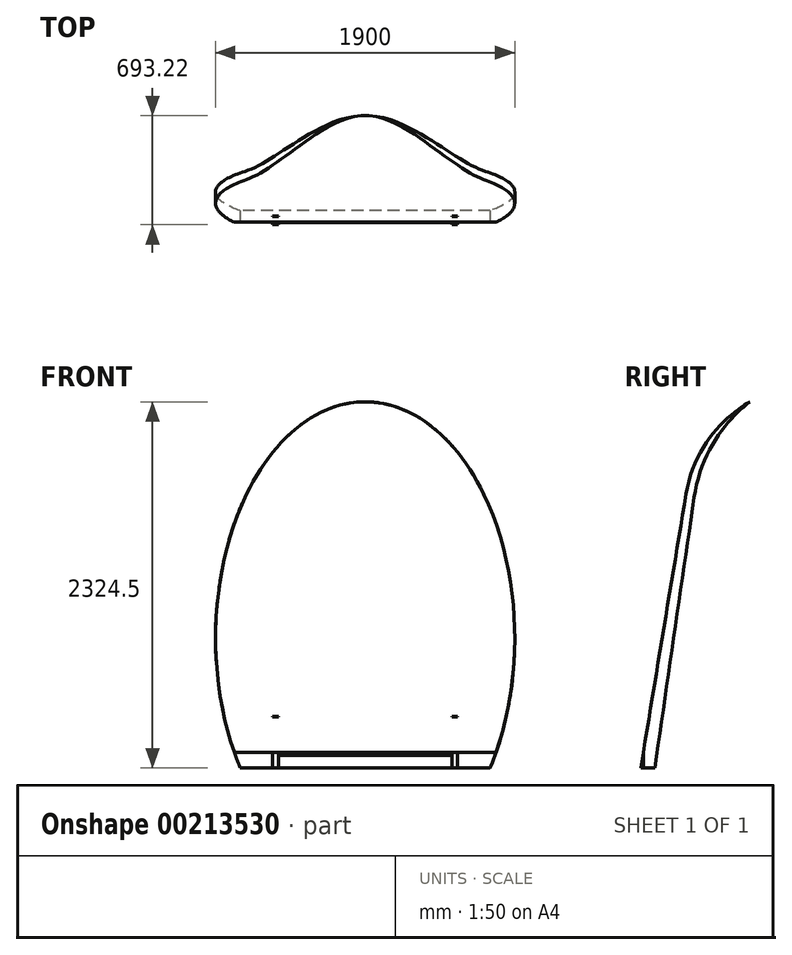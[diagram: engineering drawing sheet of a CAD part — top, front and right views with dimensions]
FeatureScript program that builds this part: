
annotation { "Feature Type Name" : "Feature", "Feature Type Description" : "" }
export const myFeature = defineFeature(function(context is Context, id is Id, definition is map)
    precondition{}
    {
        {
            var Q0;
            Q0=qCreatedBy(makeId("Top.planeOp"),FACE);
            var sketch = newSketch(context, id + "F0", { "sketchPlane" : qUnion([Q0])});
            skLineSegment(sketch, "E0.bottom", {"start": v(-1200, -1500) * mm, "end": v(-1150, -1500) * mm});
            skLineSegment(sketch, "E0.top", {"start": v(-1200, 1500) * mm, "end": v(-1150, 1500) * mm});
            skLineSegment(sketch, "E0.left", {"start": v(-1200, -1500) * mm, "end": v(-1200, 1500) * mm});
            skLineSegment(sketch, "E0.right", {"start": v(-1150, -1500) * mm, "end": v(-1150, 1500) * mm});
            skSolve(sketch);
        }
        {
            var Q0;
            Q0 = qSketchRegion(id + "F0", true);
            extrude(context, id + "F1", {"entities" : qUnion([Q0]), "depth" : 75 * mm});
        }
        {
            var Q0;
            Q0=qCreatedBy(makeId("Top.planeOp"),FACE);
            var sketch = newSketch(context, id + "F2", { "sketchPlane" : qUnion([Q0])});
            skPoint(sketch, "E1.0", {"position": v(-1175, -1500) * mm});
            skLineSegment(sketch, "E2.0", {"start": v(-1200, -1500) * mm, "end": v(-1150, -1500) * mm, "construction": true});
            skLineSegment(sketch, "E3.bottom", {"start": v(-1150, -1500) * mm, "end": v(1150, -1500) * mm});
            skLineSegment(sketch, "E3.top", {"start": v(-1150, -1450) * mm, "end": v(1150, -1450) * mm});
            skLineSegment(sketch, "E3.left", {"start": v(-1150, -1500) * mm, "end": v(-1150, -1450) * mm});
            skLineSegment(sketch, "E3.right", {"start": v(1150, -1500) * mm, "end": v(1150, -1450) * mm});
            skSolve(sketch);
        }
        {
            var Q0;
            Q0 = qSketchRegion(id + "F2", true);
            extrude(context, id + "F3", {"entities" : qUnion([Q0]), "depth" : 75 * mm});
        }
        {
            var Q0;
            Q0=qCreatedBy(makeId("Top.planeOp"),FACE);
            var sketch = newSketch(context, id + "F4", { "sketchPlane" : qUnion([Q0])});
            skLineSegment(sketch, "E4.0", {"start": v(-1150, -1500) * mm, "end": v(-1150, 1500) * mm, "construction": true});
            skLineSegment(sketch, "E5.bottom", {"start": v(-1150, -165) * mm, "end": v(1150, -165) * mm});
            skLineSegment(sketch, "E5.top", {"start": v(-1150, -115) * mm, "end": v(1150, -115) * mm});
            skLineSegment(sketch, "E5.left", {"start": v(-1150, -165) * mm, "end": v(-1150, -115) * mm});
            skLineSegment(sketch, "E5.right", {"start": v(1150, -165) * mm, "end": v(1150, -115) * mm});
            skSolve(sketch);
        }
        {
            var Q0;
            Q0 = qSketchRegion(id + "F4", true);
            extrude(context, id + "F5", {"entities" : qUnion([Q0]), "depth" : 75 * mm});
        }
        {
            var Q0;
            Q0=makeQuery(id+"F1.opExtrude","SWEPT_BODY",BODY,{"disambiguationData":[OSD([sQuery(id+"F0.wireOp",EDGE,"E0.bottom"),sQuery(id+"F0.wireOp",EDGE,"E0.top"),sQuery(id+"F0.wireOp",EDGE,"E0.left"),sQuery(id+"F0.wireOp",EDGE,"E0.right")])]});
            var Q1;
            Q1=makeQuery(id+"Fr9E7EgIBilY6Pa_3.opExtrude","SWEPT_BODY",BODY,{"disambiguationData":[OSD([sQuery(id+"FE9dtEMBFkgNXne_3.wireOp",EDGE,"NZsNCRdN-yHCd-Vyrk-8MUB-36pA6QKNkkjT.bottom"),sQuery(id+"FE9dtEMBFkgNXne_3.wireOp",EDGE,"NZsNCRdN-yHCd-Vyrk-8MUB-36pA6QKNkkjT.top"),sQuery(id+"FE9dtEMBFkgNXne_3.wireOp",EDGE,"NZsNCRdN-yHCd-Vyrk-8MUB-36pA6QKNkkjT.left"),sQuery(id+"FE9dtEMBFkgNXne_3.wireOp",EDGE,"NZsNCRdN-yHCd-Vyrk-8MUB-36pA6QKNkkjT.right")])]});
            var Q2;
            Q2=qCreatedBy(makeId("Right.planeOp"),FACE);
            mirror(context, id + "F6", {"entities" : qUnion([Q0, Q1]), "mirrorPlane" : qUnion([Q2])});
        }
        {
            var Q0;
            Q0=makeQuery(id+"F3.opExtrude","SWEPT_BODY",BODY,{"disambiguationData":[OSD([sQuery(id+"F2.wireOp",EDGE,"E3.bottom"),sQuery(id+"F2.wireOp",EDGE,"E3.top"),sQuery(id+"F2.wireOp",EDGE,"E3.left"),sQuery(id+"F2.wireOp",EDGE,"E3.right")])]});
            var Q1;
            Q1=qCreatedBy(makeId("Front.planeOp"),FACE);
            mirror(context, id + "F7", {"entities" : qUnion([Q0]), "mirrorPlane" : qUnion([Q1])});
        }
        {
            var Q0;
            Q0=qCreatedBy(makeId("Top.planeOp"),FACE);
            var sketch = newSketch(context, id + "F8", { "sketchPlane" : qUnion([Q0])});
            skLineSegment(sketch, "E6.0", {"start": v(-1150, -115) * mm, "end": v(1150, -115) * mm, "construction": true});
            skLineSegment(sketch, "E7.bottom", {"start": v(-587, -115) * mm, "end": v(-550, -115) * mm});
            skLineSegment(sketch, "E7.top", {"start": v(-587, -90) * mm, "end": v(-550, -90) * mm});
            skLineSegment(sketch, "E7.left", {"start": v(-587, -115) * mm, "end": v(-587, -90) * mm});
            skLineSegment(sketch, "E7.right", {"start": v(-550, -115) * mm, "end": v(-550, -90) * mm});
            skSolve(sketch);
        }
        {
            var Q0;
            Q0 = qSketchRegion(id + "F8", true);
            extrude(context, id + "F9", {"entities" : qUnion([Q0]), "depth" : 1000 * mm});
        }
        {
            var Q0;
            Q0=qCreatedBy(makeId("Top.planeOp"),FACE);
            var sketch = newSketch(context, id + "F10", { "sketchPlane" : qUnion([Q0])});
            skLineSegment(sketch, "E8.0", {"start": v(-1150, -115) * mm, "end": v(1150, -115) * mm});
            skLineSegment(sketch, "E9.0", {"start": v(-1150, -1500) * mm, "end": v(-1150, 1500) * mm, "construction": true});
            skLineSegment(sketch, "E10.0", {"start": v(1150, -1500) * mm, "end": v(1150, 1500) * mm, "construction": true});
            skLineSegment(sketch, "E11.bottom", {"start": v(-1150, 835) * mm, "end": v(1150, 835) * mm});
            skLineSegment(sketch, "E11.top", {"start": v(-1150, 885) * mm, "end": v(1150, 885) * mm});
            skLineSegment(sketch, "E11.left", {"start": v(-1150, 835) * mm, "end": v(-1150, 885) * mm});
            skLineSegment(sketch, "E11.right", {"start": v(1150, 835) * mm, "end": v(1150, 885) * mm});
            skSolve(sketch);
        }
        {
            var Q0;
            Q0 = qSketchRegion(id + "F10", true);
            extrude(context, id + "F11", {"entities" : qUnion([Q0]), "depth" : 75 * mm});
        }
        {
            var Q0;
            Q0=makeQuery(id+"F5.opExtrude","CAP_FACE",FACE,{"disambiguationData":[OSD([sQuery(id+"F4.wireOp",EDGE,"E5.bottom"),sQuery(id+"F4.wireOp",EDGE,"E5.top"),sQuery(id+"F4.wireOp",EDGE,"E5.left"),sQuery(id+"F4.wireOp",EDGE,"E5.right")])],"isStart":false});
            var sketch = newSketch(context, id + "F12", { "sketchPlane" : qUnion([Q0])});
            skLineSegment(sketch, "E12.0", {"start": v(-1150, 835) * mm, "end": v(1150, 835) * mm, "construction": true});
            skLineSegment(sketch, "E13.0", {"start": v(-587, -115) * mm, "end": v(-587, -90) * mm, "construction": true});
            skLineSegment(sketch, "E14.0", {"start": v(-1150, 1450) * mm, "end": v(1150, 1450) * mm, "construction": true});
            skLineSegment(sketch, "E15.top", {"start": v(-587, 1500) * mm, "end": v(-612, 1500) * mm});
            skLineSegment(sketch, "E15.left", {"start": v(-587, -165) * mm, "end": v(-587, 1500) * mm});
            skLineSegment(sketch, "E15.right", {"start": v(-612, -165) * mm, "end": v(-612, 1500) * mm});
            skLineSegment(sketch, "E16.0", {"start": v(-1150, -165) * mm, "end": v(1150, -165) * mm, "construction": true});
            skLineSegment(sketch, "E17", {"start": v(-612, -165) * mm, "end": v(-587, -165) * mm});
            skSolve(sketch);
        }
        {
            var Q0;
            Q0 = qSketchRegion(id + "F12", true);
            extrude(context, id + "F13", {"entities" : qUnion([Q0]), "depth" : 37 * mm});
        }
        {
            var Q0;
            Q0=qCreatedBy(makeId("Top.planeOp"),FACE);
            var sketch = newSketch(context, id + "F14", { "sketchPlane" : qUnion([Q0])});
            skLineSegment(sketch, "E18.0", {"start": v(-587, -165) * mm, "end": v(-587, 1500) * mm, "construction": true});
            skLineSegment(sketch, "E19.0", {"start": v(-1150, 835) * mm, "end": v(1150, 835) * mm, "construction": true});
            skLineSegment(sketch, "E20.bottom", {"start": v(-587, 835) * mm, "end": v(-550, 835) * mm});
            skLineSegment(sketch, "E20.top", {"start": v(-587, 810) * mm, "end": v(-550, 810) * mm});
            skLineSegment(sketch, "E20.left", {"start": v(-587, 835) * mm, "end": v(-587, 810) * mm});
            skLineSegment(sketch, "E20.right", {"start": v(-550, 835) * mm, "end": v(-550, 810) * mm});
            skSolve(sketch);
        }
        {
            var Q0;
            Q0 = qSketchRegion(id + "F14", true);
            extrude(context, id + "F15", {"entities" : qUnion([Q0]), "depth" : 1000 * mm});
        }
        {
            var Q0;
            Q0=makeQuery(id+"F15.opExtrude","SWEPT_FACE",FACE,{"disambiguationData":[OSD([sQuery(id+"F14.wireOp",EDGE,"E20.left")])]});
            var sketch = newSketch(context, id + "F16", { "sketchPlane" : qUnion([Q0])});
            skLineSegment(sketch, "E21.0", {"start": v(165, 112) * mm, "end": v(-1500, 112) * mm, "construction": true});
            skLineSegment(sketch, "E22", {"start": v(-1500, 112) * mm, "end": v(-1500, 3112) * mm, "construction": true});
            skLineSegment(sketch, "E23", {"start": v(-1192.7, 112) * mm, "end": v(-1192.7, 2420.61) * mm, "construction": true});
            skLineSegment(sketch, "E24.0", {"start": v(-835, 1000) * mm, "end": v(-835, 0) * mm, "construction": true});
            skLineSegment(sketch, "E25", {"start": v(-1192.7, 2420.61) * mm, "end": v(-452.72, 2420.61) * mm, "construction": true});
            skLineSegment(sketch, "E26", {"start": v(-688.07, 112) * mm, "end": v(-1070.06, 2420.61) * mm});
            skLineSegment(sketch, "E27.0", {"start": v(-724.57, 105.96) * mm, "end": v(-1106.56, 2414.57) * mm});
            skLineSegment(sketch, "E28", {"start": v(-1106.56, 2414.57) * mm, "end": v(-1070.06, 2420.61) * mm});
            skLineSegment(sketch, "E29", {"start": v(-724.57, 105.96) * mm, "end": v(-688.07, 112) * mm});
            skSolve(sketch);
        }
        {
            var Q0;
            Q0 = qSketchRegion(id + "F16", true);
            extrude(context, id + "F17", {"entities" : qUnion([Q0]), "depth" : 25 * mm});
        }
        {
            var Q0;
            Q0=makeQuery(id+"F9.opExtrude","CAP_FACE",FACE,{"disambiguationData":[OSD([sQuery(id+"F8.wireOp",EDGE,"E7.bottom"),sQuery(id+"F8.wireOp",EDGE,"E7.top"),sQuery(id+"F8.wireOp",EDGE,"E7.left"),sQuery(id+"F8.wireOp",EDGE,"E7.right")])],"isStart":false});
            var sketch = newSketch(context, id + "F18", { "sketchPlane" : qUnion([Q0])});
            skLineSegment(sketch, "E30.0", {"start": v(-587, -115) * mm, "end": v(-550, -115) * mm, "construction": true});
            skLineSegment(sketch, "E31.bottom", {"start": v(-587, -115) * mm, "end": v(-550, -115) * mm});
            skLineSegment(sketch, "E31.top", {"start": v(-587, 872.86) * mm, "end": v(-550, 872.86) * mm});
            skLineSegment(sketch, "E31.left", {"start": v(-587, -115) * mm, "end": v(-587, 872.86) * mm});
            skLineSegment(sketch, "E31.right", {"start": v(-550, -115) * mm, "end": v(-550, 872.86) * mm});
            skSolve(sketch);
        }
        {
            var Q0;
            Q0 = qSketchRegion(id + "F18", true);
            extrude(context, id + "F19", {"entities" : qUnion([Q0]), "depth" : 25 * mm});
        }
        {
            var Q0;
            Q0=makeQuery(id+"F11.opExtrude","SWEPT_FACE",FACE,{"disambiguationData":[OSD([sQuery(id+"F10.wireOp",EDGE,"E11.bottom")])]});
            var sketch = newSketch(context, id + "F20", { "sketchPlane" : qUnion([Q0])});
            skLineSegment(sketch, "E32.0", {"start": v(-1411.54, 0) * mm, "end": v(-411.41, 0) * mm, "construction": true});
            skLineSegment(sketch, "E33.0", {"start": v(-587, 1000) * mm, "end": v(-550, 1000) * mm, "construction": true});
            skLineSegment(sketch, "E34", {"start": v(-587, 1000) * mm, "end": v(-1100, 0) * mm});
            skLineSegment(sketch, "E35.0", {"start": v(-619.92, 1016.89) * mm, "end": v(-1132.92, 16.89) * mm});
            skLineSegment(sketch, "E36", {"start": v(-619.92, 1016.89) * mm, "end": v(-587, 1000) * mm});
            skLineSegment(sketch, "E37", {"start": v(-1132.92, 16.89) * mm, "end": v(-1100, 0) * mm});
            skSolve(sketch);
        }
        {
            var Q0;
            Q0 = qSketchRegion(id + "F20", true);
            extrude(context, id + "F21", {"entities" : qUnion([Q0]), "depth" : 25 * mm});
        }
        {
            var Q0;
            Q0=makeQuery(id+"F5.opExtrude","CAP_FACE",FACE,{"disambiguationData":[OSD([sQuery(id+"F4.wireOp",EDGE,"E5.bottom"),sQuery(id+"F4.wireOp",EDGE,"E5.top"),sQuery(id+"F4.wireOp",EDGE,"E5.left"),sQuery(id+"F4.wireOp",EDGE,"E5.right")])],"isStart":false});
            var sketch = newSketch(context, id + "F22", { "sketchPlane" : qUnion([Q0])});
            skLineSegment(sketch, "E38.0", {"start": v(-1150, 885) * mm, "end": v(1150, 885) * mm, "construction": true});
            skLineSegment(sketch, "E39.0", {"start": v(-612, 688.07) * mm, "end": v(-612, 1070.06) * mm, "construction": true});
            skLineSegment(sketch, "E40.0", {"start": v(-1150, -1500) * mm, "end": v(1150, -1500) * mm, "construction": true});
            skLineSegment(sketch, "E41", {"start": v(-612, 885) * mm, "end": v(-1081.1, -1500) * mm});
            skLineSegment(sketch, "E42.0", {"start": v(-636.43, 890.33) * mm, "end": v(-1105.52, -1494.67) * mm});
            skLineSegment(sketch, "E43", {"start": v(-1105.52, -1494.67) * mm, "end": v(-1081.1, -1500) * mm});
            skLineSegment(sketch, "E44", {"start": v(-636.43, 890.33) * mm, "end": v(-612, 885) * mm});
            skSolve(sketch);
        }
        {
            var Q0;
            Q0 = qSketchRegion(id + "F22", true);
            extrude(context, id + "F23", {"entities" : qUnion([Q0]), "depth" : 37 * mm});
        }
        {
            var Q0;
            Q0=makeQuery(id+"F11.opExtrude","CAP_FACE",FACE,{"disambiguationData":[OSD([sQuery(id+"F10.wireOp",EDGE,"E11.bottom"),sQuery(id+"F10.wireOp",EDGE,"E11.top"),sQuery(id+"F10.wireOp",EDGE,"E11.left"),sQuery(id+"F10.wireOp",EDGE,"E11.right")])],"isStart":false});
            var sketch = newSketch(context, id + "F24", { "sketchPlane" : qUnion([Q0])});
            skLineSegment(sketch, "E45.0", {"start": v(-1150, 1500) * mm, "end": v(1150, 1500) * mm, "construction": true});
            skLineSegment(sketch, "E46.0", {"start": v(-636.43, 890.33) * mm, "end": v(-1105.52, -1494.67) * mm, "construction": true});
            skLineSegment(sketch, "E47", {"start": v(-647.31, 835) * mm, "end": v(-825.9, 1500) * mm});
            skLineSegment(sketch, "E48.0", {"start": v(-671.9, 830.15) * mm, "end": v(-850.49, 1495.15) * mm});
            skLineSegment(sketch, "E49", {"start": v(-850.49, 1495.15) * mm, "end": v(-825.9, 1500) * mm});
            skLineSegment(sketch, "E50", {"start": v(-671.9, 830.15) * mm, "end": v(-647.31, 835) * mm});
            skSolve(sketch);
        }
        {
            var Q0;
            Q0 = qSketchRegion(id + "F24", true);
            extrude(context, id + "F25", {"entities" : qUnion([Q0]), "depth" : 37 * mm});
        }
        {
            var Q0;
            Q0=makeQuery(id+"F9.opExtrude","SWEPT_FACE",FACE,{"disambiguationData":[OSD([sQuery(id+"F8.wireOp",EDGE,"E7.right")])]});
            var sketch = newSketch(context, id + "F26", { "sketchPlane" : qUnion([Q0])});
            skLineSegment(sketch, "E51.0", {"start": v(-115, 1000) * mm, "end": v(-115, 0) * mm, "construction": true});
            skLineSegment(sketch, "E52.0", {"start": v(835, 1000) * mm, "end": v(835, 0) * mm, "construction": true});
            skLineSegment(sketch, "E53.bottom", {"start": v(-115, 792) * mm, "end": v(835, 792) * mm});
            skLineSegment(sketch, "E53.top", {"start": v(-115, 755) * mm, "end": v(835, 755) * mm});
            skLineSegment(sketch, "E53.left", {"start": v(-115, 792) * mm, "end": v(-115, 755) * mm});
            skLineSegment(sketch, "E53.right", {"start": v(835, 792) * mm, "end": v(835, 755) * mm});
            skSolve(sketch);
        }
        {
            var Q0;
            Q0 = qSketchRegion(id + "F26", true);
            extrude(context, id + "F27", {"entities" : qUnion([Q0]), "depth" : 25 * mm});
        }
        {
            var Q0;
            Q0=makeQuery(id+"F9.opExtrude","SWEPT_EDGE",EDGE,{"disambiguationData":[OSD([sQuery(id+"F8.wireOp",EDGE,"E7.bottom"),sQuery(id+"F8.wireOp",EDGE,"E7.left")])]});
            cPlane(context, id + "F28", {"entities" : qUnion([Q0]), "cplaneType" : CPlaneType.LINE_ANGLE, "offset" : 25 * mm, "angle" : 45 * degree, "width" : 150 * mm, "height" : 150 * mm});
        }
        {
            var Q0;
            Q0=qCreatedBy(id+"F28.planeOp",FACE);
            var sketch = newSketch(context, id + "F29", { "sketchPlane" : qUnion([Q0])});
            skLineSegment(sketch, "E54", {"start": v(886.66, 112) * mm, "end": v(886.66, 75) * mm, "construction": true});
            skLineSegment(sketch, "E55.0", {"start": v(496.39, 1000) * mm, "end": v(496.39, 0) * mm, "construction": true});
            skLineSegment(sketch, "E56", {"start": v(496.39, 1000) * mm, "end": v(886.66, 112) * mm});
            skLineSegment(sketch, "E57.0", {"start": v(529.58, 1016.44) * mm, "end": v(919.85, 128.44) * mm});
            skLineSegment(sketch, "E58", {"start": v(496.39, 1000) * mm, "end": v(529.58, 1016.44) * mm});
            skLineSegment(sketch, "E59", {"start": v(919.85, 128.44) * mm, "end": v(886.66, 112) * mm});
            skSolve(sketch);
        }
        {
            var Q0;
            Q0 = qSketchRegion(id + "F29", true);
            extrude(context, id + "F30", {"entities" : qUnion([Q0]), "depth" : 25 * mm});
        }
        {
            var Q0;
            Q0=makeQuery(id+"F19.opExtrude","SWEPT_EDGE",EDGE,{"disambiguationData":[OSD([sQuery(id+"F18.wireOp",EDGE,"E31.top"),sQuery(id+"F18.wireOp",EDGE,"E31.right")])]});
            cPlane(context, id + "F31", {"entities" : qUnion([Q0]), "cplaneType" : CPlaneType.LINE_ANGLE, "offset" : 25 * mm, "angle" : 155 * degree, "width" : 150 * mm, "height" : 150 * mm});
        }
        {
            var Q0;
            Q0=qCreatedBy(id+"F31.planeOp",FACE);
            var sketch = newSketch(context, id + "F32", { "sketchPlane" : qUnion([Q0])});
            skLineSegment(sketch, "E60.0", {"start": v(1023.52, 1025) * mm, "end": v(1023.52, 1000) * mm, "construction": true});
            skLineSegment(sketch, "E61", {"start": v(1623.22, 75) * mm, "end": v(1623.22, 112) * mm, "construction": true});
            skLineSegment(sketch, "E62", {"start": v(1023.52, 1000) * mm, "end": v(1623.22, 112) * mm});
            skLineSegment(sketch, "E63.0", {"start": v(1053.01, 1022.44) * mm, "end": v(1652.71, 134.44) * mm});
            skLineSegment(sketch, "E64", {"start": v(1023.52, 1000) * mm, "end": v(1053.01, 1022.44) * mm});
            skLineSegment(sketch, "E65", {"start": v(1623.22, 112) * mm, "end": v(1652.71, 134.44) * mm});
            skSolve(sketch);
        }
        {
            var Q0;
            Q0 = qSketchRegion(id + "F32", true);
            extrude(context, id + "F33", {"entities" : qUnion([Q0]), "oppositeDirection" : true, "depth" : 25 * mm});
        }
        {
            var Q0;
            Q0=makeQuery(id+"F33.opExtrude","SWEPT_BODY",BODY,{"disambiguationData":[OSD([sQuery(id+"F32.wireOp",EDGE,"E62"),sQuery(id+"F32.wireOp",EDGE,"E63.0"),sQuery(id+"F32.wireOp",EDGE,"E64"),sQuery(id+"F32.wireOp",EDGE,"E65")])]});
            var Q1;
            Q1=makeQuery(id+"F13.opExtrude","SWEPT_BODY",BODY,{"disambiguationData":[OSD([sQuery(id+"F12.wireOp",EDGE,"E15.top"),sQuery(id+"F12.wireOp",EDGE,"E15.left"),sQuery(id+"F12.wireOp",EDGE,"E15.right"),sQuery(id+"F12.wireOp",EDGE,"E17")])]});
            var Q2;
            Q2=makeQuery(id+"F25.opExtrude","SWEPT_BODY",BODY,{"disambiguationData":[OSD([sQuery(id+"F24.wireOp",EDGE,"E47"),sQuery(id+"F24.wireOp",EDGE,"E48.0"),sQuery(id+"F24.wireOp",EDGE,"E49"),sQuery(id+"F24.wireOp",EDGE,"E50")])]});
            var Q3;
            Q3=makeQuery(id+"F23.opExtrude","SWEPT_BODY",BODY,{"disambiguationData":[OSD([sQuery(id+"F22.wireOp",EDGE,"E41"),sQuery(id+"F22.wireOp",EDGE,"E42.0"),sQuery(id+"F22.wireOp",EDGE,"E43"),sQuery(id+"F22.wireOp",EDGE,"E44")])]});
            var Q4;
            Q4=makeQuery(id+"F21.opExtrude","SWEPT_BODY",BODY,{"disambiguationData":[OSD([sQuery(id+"F20.wireOp",EDGE,"E34"),sQuery(id+"F20.wireOp",EDGE,"E35.0"),sQuery(id+"F20.wireOp",EDGE,"E36"),sQuery(id+"F20.wireOp",EDGE,"E37")])]});
            var Q5;
            Q5=makeQuery(id+"F15.opExtrude","SWEPT_BODY",BODY,{"disambiguationData":[OSD([sQuery(id+"F14.wireOp",EDGE,"E20.bottom"),sQuery(id+"F14.wireOp",EDGE,"E20.top"),sQuery(id+"F14.wireOp",EDGE,"E20.left"),sQuery(id+"F14.wireOp",EDGE,"E20.right")])]});
            var Q6;
            Q6=makeQuery(id+"F17.opExtrude","SWEPT_BODY",BODY,{"disambiguationData":[OSD([sQuery(id+"F16.wireOp",EDGE,"E26"),sQuery(id+"F16.wireOp",EDGE,"E27.0"),sQuery(id+"F16.wireOp",EDGE,"E28"),sQuery(id+"F16.wireOp",EDGE,"E29")])]});
            var Q7;
            Q7=makeQuery(id+"F27.opExtrude","SWEPT_BODY",BODY,{"disambiguationData":[OSD([sQuery(id+"F26.wireOp",EDGE,"E53.bottom"),sQuery(id+"F26.wireOp",EDGE,"E53.top"),sQuery(id+"F26.wireOp",EDGE,"E53.left"),sQuery(id+"F26.wireOp",EDGE,"E53.right")])]});
            var Q8;
            Q8=makeQuery(id+"F19.opExtrude","SWEPT_BODY",BODY,{"disambiguationData":[OSD([sQuery(id+"F18.wireOp",EDGE,"E31.bottom"),sQuery(id+"F18.wireOp",EDGE,"E31.top"),sQuery(id+"F18.wireOp",EDGE,"E31.left"),sQuery(id+"F18.wireOp",EDGE,"E31.right")])]});
            var Q9;
            Q9=makeQuery(id+"F9.opExtrude","SWEPT_BODY",BODY,{"disambiguationData":[OSD([sQuery(id+"F8.wireOp",EDGE,"E7.bottom"),sQuery(id+"F8.wireOp",EDGE,"E7.top"),sQuery(id+"F8.wireOp",EDGE,"E7.left"),sQuery(id+"F8.wireOp",EDGE,"E7.right")])]});
            var Q10;
            Q10=makeQuery(id+"F30.opExtrude","SWEPT_BODY",BODY,{"disambiguationData":[OSD([sQuery(id+"F29.wireOp",EDGE,"E56"),sQuery(id+"F29.wireOp",EDGE,"E57.0"),sQuery(id+"F29.wireOp",EDGE,"E58"),sQuery(id+"F29.wireOp",EDGE,"E59")])]});
            var Q11;
            Q11=qCreatedBy(makeId("Right.planeOp"),FACE);
            mirror(context, id + "F34", {"entities" : qUnion([Q0, Q1, Q2, Q3, Q4, Q5, Q6, Q7, Q8, Q9, Q10]), "mirrorPlane" : qUnion([Q11])});
        }
        {
            var Q0;
            Q0=makeQuery(id+"F27.opExtrude","SWEPT_FACE",FACE,{"disambiguationData":[OSD([sQuery(id+"F26.wireOp",EDGE,"E53.bottom")])]});
            var sketch = newSketch(context, id + "F35", { "sketchPlane" : qUnion([Q0])});
            skLineSegment(sketch, "E66.0", {"start": v(-525, -115) * mm, "end": v(-525, 835) * mm, "construction": true});
            skLineSegment(sketch, "E67.0", {"start": v(525, -115) * mm, "end": v(525, 835) * mm, "construction": true});
            skLineSegment(sketch, "E68.bottom", {"start": v(-525, -115) * mm, "end": v(525, -115) * mm});
            skLineSegment(sketch, "E68.top", {"start": v(-525, -90) * mm, "end": v(525, -90) * mm});
            skLineSegment(sketch, "E68.left", {"start": v(-525, -115) * mm, "end": v(-525, -90) * mm});
            skLineSegment(sketch, "E68.right", {"start": v(525, -115) * mm, "end": v(525, -90) * mm});
            skSolve(sketch);
        }
        {
            var Q0;
            Q0 = qSketchRegion(id + "F35", true);
            extrude(context, id + "F36", {"entities" : qUnion([Q0]), "oppositeDirection" : true, "depth" : 37 * mm});
        }
        {
            var Q0;
            Q0=makeQuery(id+"F27.opExtrude","SWEPT_FACE",FACE,{"disambiguationData":[OSD([sQuery(id+"F26.wireOp",EDGE,"E53.bottom")])]});
            var sketch = newSketch(context, id + "F37", { "sketchPlane" : qUnion([Q0])});
            skLineSegment(sketch, "E69.0", {"start": v(-525, -115) * mm, "end": v(-525, 835) * mm, "construction": true});
            skLineSegment(sketch, "E70.0", {"start": v(525, -115) * mm, "end": v(525, 835) * mm, "construction": true});
            skLineSegment(sketch, "E71.bottom", {"start": v(-525, 835) * mm, "end": v(525, 835) * mm});
            skLineSegment(sketch, "E71.top", {"start": v(-525, 810) * mm, "end": v(525, 810) * mm});
            skLineSegment(sketch, "E71.left", {"start": v(-525, 835) * mm, "end": v(-525, 810) * mm});
            skLineSegment(sketch, "E71.right", {"start": v(525, 835) * mm, "end": v(525, 810) * mm});
            skSolve(sketch);
        }
        {
            var Q0;
            Q0 = qSketchRegion(id + "F37", true);
            extrude(context, id + "F38", {"entities" : qUnion([Q0]), "oppositeDirection" : true, "depth" : 37 * mm});
        }
        {
            var Q0;
            Q0=makeQuery(id+"F34.opPattern","COPY",FACE,{"derivedFrom":makeQuery(id+"F15.opExtrude","SWEPT_FACE",FACE,{"disambiguationData":[OSD([sQuery(id+"F14.wireOp",EDGE,"E20.bottom")])]}),"instanceName":"1"});
            var sketch = newSketch(context, id + "F39", { "sketchPlane" : qUnion([Q0])});
            skLineSegment(sketch, "E72", {"start": v(0, 0) * mm, "end": v(0, 3000) * mm, "construction": true});
            skEllipse(sketch, "E73", {"center": v(0, 1500) * mm, "majorRadius": 1500 * mm, "minorRadius": 950 * mm, "majorAxis": v(0, 1)});
            skSolve(sketch);
        }
        {
            var Q0;
            Q0 = qSketchRegion(id + "F39", true);
            extrude(context, id + "F40", {"entities" : qUnion([Q0]), "depth" : 680 * mm});
        }
        {
            var Q0;
            Q0=qCreatedBy(makeId("Right.planeOp"),FACE);
            var sketch = newSketch(context, id + "F41", { "sketchPlane" : qUnion([Q0])});
            skArc(sketch, "E74", {"start": v(1511.94, 2999.47) * mm, "mid": v(1243.53, 2752.57) * mm, "end": v(1106.56, 2414.57) * mm});
            skArc(sketch, "E75", {"start": v(1511.94, 2999.47) * mm, "mid": v(1275.88, 2730.39) * mm, "end": v(1157.8, 2392.47) * mm});
            skLineSegment(sketch, "E76", {"start": v(1157.8, 2392.47) * mm, "end": v(908.47, 674.97) * mm});
            skPoint(sketch, "E77.orphan", {"position": v(724.57, 105.96) * mm});
            skLineSegment(sketch, "E78", {"start": v(818.72, 674.97) * mm, "end": v(908.47, 674.97) * mm});
            skLineSegment(sketch, "E79.trimOffspring", {"start": v(818.72, 674.97) * mm, "end": v(1106.56, 2414.57) * mm});
            skSolve(sketch);
        }
        {
            var Q0;
            Q0 = qSketchRegion(id + "F41", true);
            extrude(context, id + "F42", {"entities" : qUnion([Q0]), "operationType" : NewBodyOperationType.INTERSECT, "endBound" : BoundingType.SYMMETRIC, "depth" : 2080 * mm});
        }
        {
            var Q0;
            Q0=makeQuery(id+"F21.opExtrude","SWEPT_BODY",BODY,{"disambiguationData":[OSD([sQuery(id+"F20.wireOp",EDGE,"E34"),sQuery(id+"F20.wireOp",EDGE,"E35.0"),sQuery(id+"F20.wireOp",EDGE,"E36"),sQuery(id+"F20.wireOp",EDGE,"E37")])]});
            var Q1;
            Q1=makeQuery(id+"F23.opExtrude","SWEPT_BODY",BODY,{"disambiguationData":[OSD([sQuery(id+"F22.wireOp",EDGE,"E41"),sQuery(id+"F22.wireOp",EDGE,"E42.0"),sQuery(id+"F22.wireOp",EDGE,"E43"),sQuery(id+"F22.wireOp",EDGE,"E44")])]});
            var Q2;
            Q2=makeQuery(id+"F25.opExtrude","SWEPT_BODY",BODY,{"disambiguationData":[OSD([sQuery(id+"F24.wireOp",EDGE,"E47"),sQuery(id+"F24.wireOp",EDGE,"E48.0"),sQuery(id+"F24.wireOp",EDGE,"E49"),sQuery(id+"F24.wireOp",EDGE,"E50")])]});
            var Q3;
            Q3=makeQuery(id+"F30.opExtrude","SWEPT_BODY",BODY,{"disambiguationData":[OSD([sQuery(id+"F29.wireOp",EDGE,"E56"),sQuery(id+"F29.wireOp",EDGE,"E57.0"),sQuery(id+"F29.wireOp",EDGE,"E58"),sQuery(id+"F29.wireOp",EDGE,"E59")])]});
            var Q4;
            Q4=makeQuery(id+"F33.opExtrude","SWEPT_BODY",BODY,{"disambiguationData":[OSD([sQuery(id+"F32.wireOp",EDGE,"E62"),sQuery(id+"F32.wireOp",EDGE,"E63.0"),sQuery(id+"F32.wireOp",EDGE,"E64"),sQuery(id+"F32.wireOp",EDGE,"E65")])]});
            deleteBodies(context, id + "F43", {"entities" : qUnion([Q0, Q1, Q2, Q3, Q4])});
        }
        {
            var Q0;
            Q0=makeQuery(id+"F34.opPattern","COPY",BODY,{"derivedFrom":makeQuery(id+"F21.opExtrude","SWEPT_BODY",BODY,{"disambiguationData":[OSD([sQuery(id+"F20.wireOp",EDGE,"E34"),sQuery(id+"F20.wireOp",EDGE,"E35.0"),sQuery(id+"F20.wireOp",EDGE,"E36"),sQuery(id+"F20.wireOp",EDGE,"E37")])]}),"instanceName":"1"});
            var Q1;
            Q1=makeQuery(id+"F34.opPattern","COPY",BODY,{"derivedFrom":makeQuery(id+"F23.opExtrude","SWEPT_BODY",BODY,{"disambiguationData":[OSD([sQuery(id+"F22.wireOp",EDGE,"E41"),sQuery(id+"F22.wireOp",EDGE,"E42.0"),sQuery(id+"F22.wireOp",EDGE,"E43"),sQuery(id+"F22.wireOp",EDGE,"E44")])]}),"instanceName":"1"});
            var Q2;
            Q2=makeQuery(id+"F34.opPattern","COPY",BODY,{"derivedFrom":makeQuery(id+"F30.opExtrude","SWEPT_BODY",BODY,{"disambiguationData":[OSD([sQuery(id+"F29.wireOp",EDGE,"E56"),sQuery(id+"F29.wireOp",EDGE,"E57.0"),sQuery(id+"F29.wireOp",EDGE,"E58"),sQuery(id+"F29.wireOp",EDGE,"E59")])]}),"instanceName":"1"});
            var Q3;
            Q3=makeQuery(id+"F34.opPattern","COPY",BODY,{"derivedFrom":makeQuery(id+"F25.opExtrude","SWEPT_BODY",BODY,{"disambiguationData":[OSD([sQuery(id+"F24.wireOp",EDGE,"E47"),sQuery(id+"F24.wireOp",EDGE,"E48.0"),sQuery(id+"F24.wireOp",EDGE,"E49"),sQuery(id+"F24.wireOp",EDGE,"E50")])]}),"instanceName":"1"});
            deleteBodies(context, id + "F44", {"entities" : qUnion([Q0, Q1, Q2, Q3])});
        }
        {
            var Q0;
            Q0=makeQuery(id+"F34.opPattern","COPY",BODY,{"derivedFrom":makeQuery(id+"F33.opExtrude","SWEPT_BODY",BODY,{"disambiguationData":[OSD([sQuery(id+"F32.wireOp",EDGE,"E62"),sQuery(id+"F32.wireOp",EDGE,"E63.0"),sQuery(id+"F32.wireOp",EDGE,"E64"),sQuery(id+"F32.wireOp",EDGE,"E65")])]}),"instanceName":"1"});
            deleteBodies(context, id + "F45", {"entities" : qUnion([Q0])});
        }
    });
